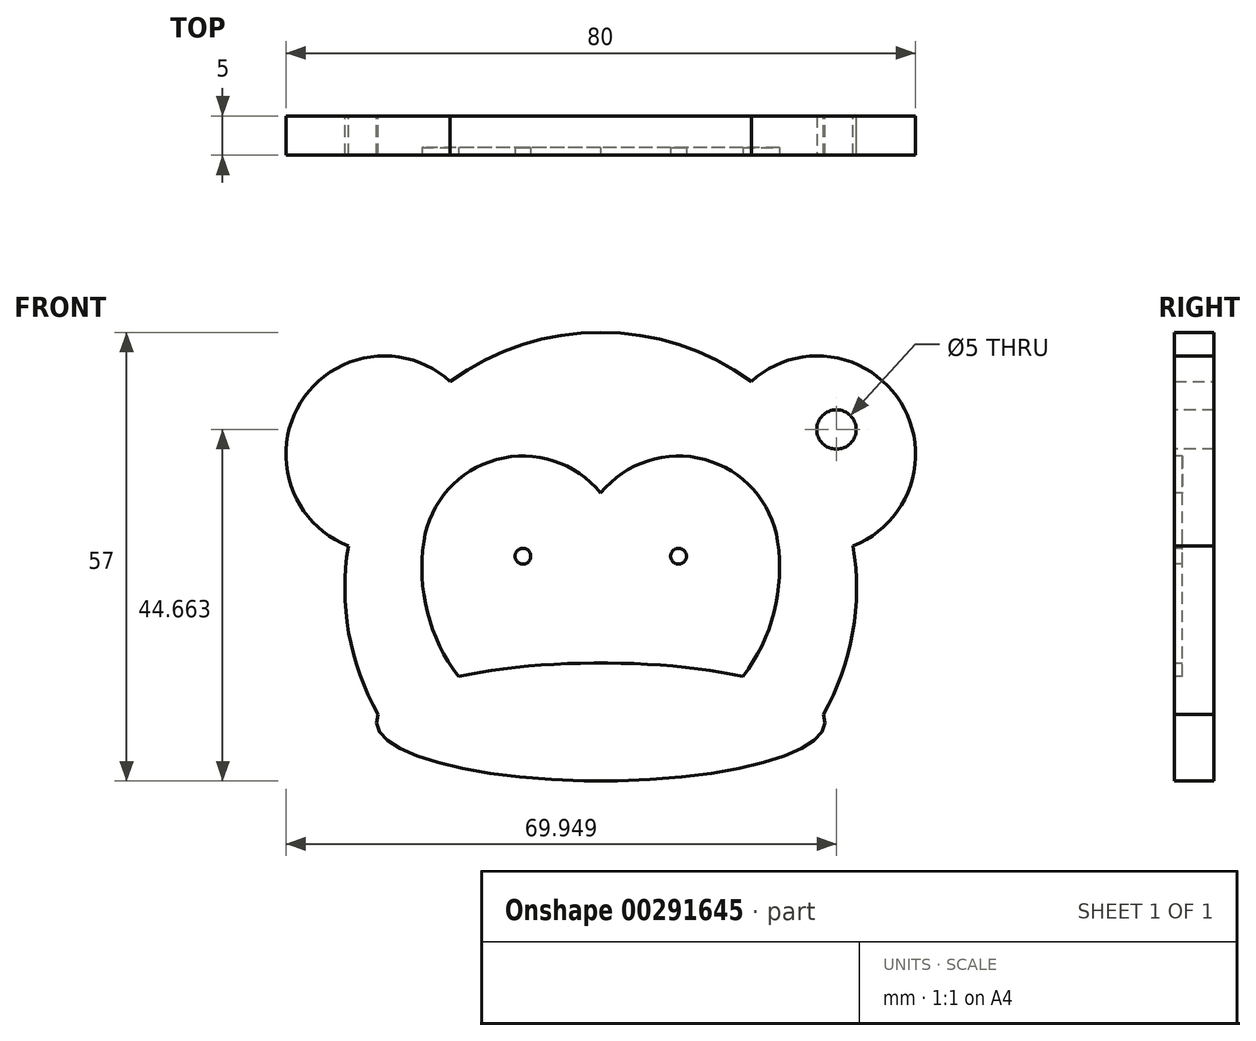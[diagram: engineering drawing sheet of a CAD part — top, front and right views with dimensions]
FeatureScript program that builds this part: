
annotation { "Feature Type Name" : "Feature", "Feature Type Description" : "" }
export const myFeature = defineFeature(function(context is Context, id is Id, definition is map)
    precondition{}
    {
        {
            var Q0;
            Q0=qCreatedBy(makeId("Front.planeOp"),FACE);
            var sketch = newSketch(context, id + "F0", { "sketchPlane" : qUnion([Q0])});
            skArc(sketch, "E0", {"start": v(-32.06, 5.36) * mm, "mid": v(-32, -5.67) * mm, "end": v(-28.27, -16.04) * mm});
            skArc(sketch, "E1", {"start": v(-19.12, 26.28) * mm, "mid": v(-38.13, 23.57) * mm, "end": v(-32.06, 5.36) * mm});
            skArc(sketch, "E2", {"start": v(32.06, 5.36) * mm, "mid": v(38.13, 23.57) * mm, "end": v(19.12, 26.28) * mm});
            skPoint(sketch, "E3.center.orphan", {"position": v(0, -17) * mm});
            skEllipse(sketch, "E4", {"center": v(0, -17) * mm, "majorRadius": 28.5 * mm, "minorRadius": 7.5 * mm, "majorAxis": v(1, 0)});
            skArc(sketch, "E5.trimOffspring", {"start": v(19.12, 26.28) * mm, "mid": v(0, 32.5) * mm, "end": v(-19.12, 26.28) * mm});
            skArc(sketch, "E6.trimOffspring", {"start": v(28.27, -16.04) * mm, "mid": v(32, -5.67) * mm, "end": v(32.06, 5.36) * mm});
            skSolve(sketch);
        }
        {
            var Q0;
            Q0 = qSketchRegion(id + "F0", true);
            extrude(context, id + "F1", {"entities" : qUnion([Q0]), "depth" : 5 * mm});
        }
        {
            var Q0;
            Q0=makeQuery(id+"F1.opExtrude","CAP_FACE",FACE,{"disambiguationData":[OSD([sQuery(id+"F0.wireOp",EDGE,"E0"),sQuery(id+"F0.wireOp",EDGE,"E1"),sQuery(id+"F0.wireOp",EDGE,"E2"),sQuery(id+"F0.wireOp",EDGE,"E4"),sQuery(id+"F0.wireOp",EDGE,"E5.trimOffspring"),sQuery(id+"F0.wireOp",EDGE,"E6.trimOffspring")])],"isStart":false});
            var sketch = newSketch(context, id + "F2", { "sketchPlane" : qUnion([Q0])});
            skArc(sketch, "E7", {"start": v(-22.74, 6) * mm, "mid": v(-22.3, -3.07) * mm, "end": v(-18.37, -11.27) * mm});
            skArc(sketch, "E8", {"start": v(0, 12.5) * mm, "mid": v(-13.46, 16.56) * mm, "end": v(-22.74, 6) * mm});
            skArc(sketch, "E9.MirrorCS", {"start": v(0, 12.5) * mm, "mid": v(13.46, 16.56) * mm, "end": v(22.74, 6) * mm});
            skArc(sketch, "E10.MirrorCS", {"start": v(22.74, 6) * mm, "mid": v(22.3, -3.07) * mm, "end": v(18.37, -11.27) * mm});
            skCircle(sketch, "E11", {"center": v(-9.89, 4.06) * mm, "radius": 1 * mm});
            skCircle(sketch, "E12", {"center": v(9.89, 4.06) * mm, "radius": 1 * mm});
            skArc(sketch, "E13.0", {"start": v(-22.47, 5.96) * mm, "mid": v(-22.01, -3.07) * mm, "end": v(-18.08, -11.2) * mm});
            skArc(sketch, "E13.1", {"start": v(0, 12.07) * mm, "mid": v(-13.23, 16.34) * mm, "end": v(-22.47, 5.96) * mm});
            skArc(sketch, "E13.2", {"start": v(0, 12.07) * mm, "mid": v(13.23, 16.34) * mm, "end": v(22.47, 5.96) * mm});
            skArc(sketch, "E13.3", {"start": v(22.47, 5.96) * mm, "mid": v(22.01, -3.07) * mm, "end": v(18.08, -11.2) * mm});
            skEllipse(sketch, "E14", {"center": v(0, -17) * mm, "majorRadius": 28.5 * mm, "minorRadius": 7.5 * mm, "majorAxis": v(1, 0)});
            skFitSpline(sketch, "E15.0", {"points": [v(28.14, -17.64) * mm, v(28.26, -17) * mm, v(28.14, -16.36) * mm, v(27.77, -15.7) * mm, v(27.13, -15.03) * mm, v(26.23, -14.36) * mm, v(25.06, -13.71) * mm, v(23.65, -13.1) * mm, v(22.27, -12.6) * mm, v(21.06, -12.23) * mm, v(20.1, -11.96) * mm, v(19.07, -11.7) * mm, v(17.66, -11.39) * mm, v(15.79, -11.02) * mm, v(13.4, -10.65) * mm, v(10.9, -10.33) * mm, v(8.28, -10.09) * mm, v(5.58, -9.9) * mm, v(3.28, -9.82) * mm, v(1.41, -9.78) * mm, v(0, -9.77) * mm, v(-1.41, -9.78) * mm, v(-3.28, -9.82) * mm, v(-5.58, -9.9) * mm, v(-8.28, -10.09) * mm, v(-10.9, -10.33) * mm, v(-13.4, -10.65) * mm, v(-15.79, -11.02) * mm, v(-17.66, -11.39) * mm, v(-19.07, -11.7) * mm, v(-20.1, -11.96) * mm, v(-21.06, -12.23) * mm, v(-22.27, -12.6) * mm, v(-23.65, -13.1) * mm, v(-25.06, -13.71) * mm, v(-26.23, -14.36) * mm, v(-27.13, -15.03) * mm, v(-27.77, -15.7) * mm, v(-28.14, -16.36) * mm, v(-28.26, -17) * mm, v(-28.14, -17.64) * mm, v(-27.77, -18.3) * mm, v(-27.13, -18.97) * mm, v(-26.23, -19.64) * mm, v(-25.06, -20.29) * mm, v(-23.65, -20.9) * mm, v(-22.27, -21.4) * mm, v(-21.06, -21.77) * mm, v(-20.1, -22.04) * mm, v(-19.07, -22.3) * mm, v(-17.66, -22.61) * mm, v(-15.79, -22.98) * mm, v(-13.4, -23.35) * mm, v(-10.9, -23.67) * mm, v(-8.28, -23.91) * mm, v(-5.58, -24.1) * mm, v(-3.28, -24.18) * mm, v(-1.41, -24.22) * mm, v(0, -24.23) * mm, v(1.41, -24.22) * mm, v(3.28, -24.18) * mm, v(5.58, -24.1) * mm, v(8.28, -23.91) * mm, v(10.9, -23.67) * mm, v(13.4, -23.35) * mm, v(15.79, -22.98) * mm, v(17.66, -22.61) * mm, v(19.07, -22.3) * mm, v(20.1, -22.04) * mm, v(21.06, -21.77) * mm, v(22.27, -21.4) * mm, v(23.65, -20.9) * mm, v(25.06, -20.29) * mm, v(26.23, -19.64) * mm, v(27.13, -18.97) * mm, v(27.77, -18.3) * mm, v(28.14, -17.64) * mm, v(28.26, -17) * mm, v(28.14, -16.36) * mm, v(28.14, -17.64) * mm]});
            skSolve(sketch);
        }
        {
            var Q0;
            Q0=makeQuery(id+"F2.imprint","IMPRINT",FACE,{"disambiguationData":[TD([[makeQuery(id+"F2.imprint","IMPRINT",EDGE,{"derivedFrom":sQuery(id+"F2.wireOp",EDGE,"E11")}),-1.0]])]});
            var sketch = newSketch(context, id + "F3", { "sketchPlane" : qUnion([Q0])});
            skSolve(sketch);
        }
        {
            var Q0;
            Q0=makeQuery(id+"F3.imprint","IMPRINT",FACE,{"disambiguationData":[TD([[makeQuery(id+"F3.imprint","IMPRINT",EDGE,{"derivedFrom":makeQuery(id+"F2.imprint","IMPRINT",EDGE,{"derivedFrom":sQuery(id+"F2.wireOp",EDGE,"E11")})}),-1.0]])]});
            extrude(context, id + "F4", {"entities" : qUnion([Q0]), "operationType" : NewBodyOperationType.REMOVE, "oppositeDirection" : true, "depth" : 1 * mm});
        }
        {
            var Q0;
            {var subQ0=sQuery(id+"F0.wireOp",EDGE,"E1");var subQ1=sQuery(id+"F0.wireOp",EDGE,"E6.trimOffspring");var subQ2=sQuery(id+"F0.wireOp",EDGE,"E5.trimOffspring");var subQ3=sQuery(id+"F0.wireOp",EDGE,"E0");var subQ4=sQuery(id+"F0.wireOp",EDGE,"E4");var subQ5=sQuery(id+"F0.wireOp",EDGE,"E2");Q0=makeQuery(id+"F4.boolean.opBoolean","SPLIT",FACE,{"disambiguationData":[TD([makeQuery(id+"F1.opExtrude","SWEPT_FACE",FACE,{"disambiguationData":[OSD([subQ3])]})])],"derivedFrom":makeQuery(id+"F1.opExtrude","CAP_FACE",FACE,{"disambiguationData":[OSD([subQ3,subQ0,subQ5,subQ4,subQ2,subQ1])],"isStart":false})});}
            var sketch = newSketch(context, id + "F5", { "sketchPlane" : qUnion([Q0])});
            skCircle(sketch, "E16", {"center": v(29.95, 20.16) * mm, "radius": 2.5 * mm});
            skSolve(sketch);
        }
        {
            var Q0;
            Q0=makeQuery(id+"F5.imprint","IMPRINT",FACE,{"disambiguationData":[TD([[makeQuery(id+"F5.imprint","IMPRINT",EDGE,{"derivedFrom":sQuery(id+"F5.wireOp",EDGE,"E16")}),1.0]])]});
            extrude(context, id + "F6", {"entities" : qUnion([Q0]), "operationType" : NewBodyOperationType.REMOVE, "endBound" : BoundingType.THROUGH_ALL, "oppositeDirection" : true, "depth" : 10 * mm});
        }
    });
